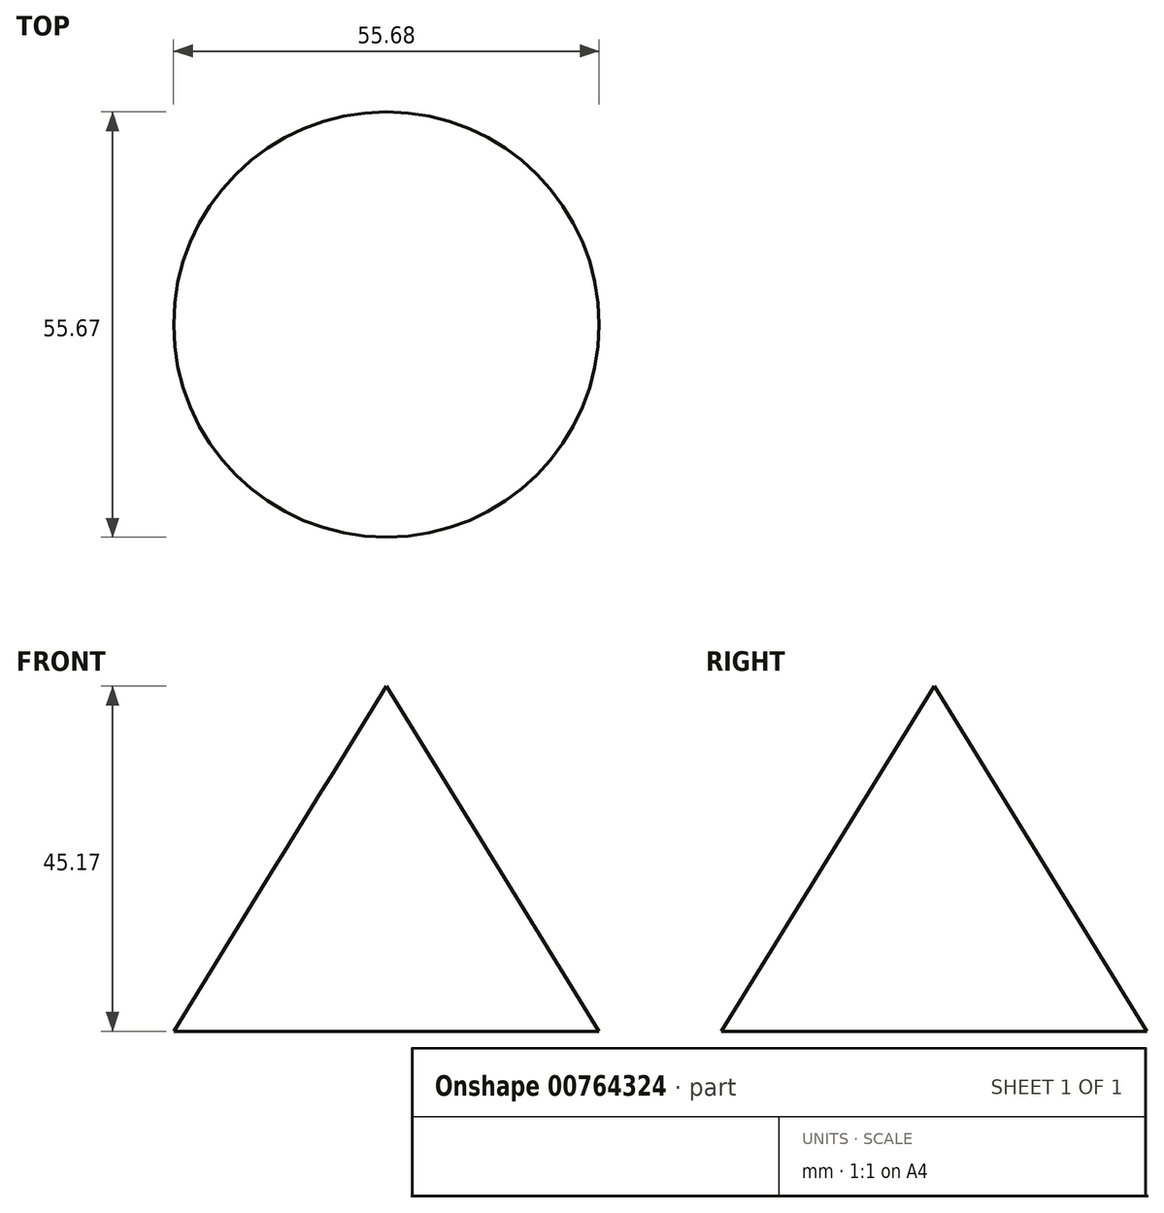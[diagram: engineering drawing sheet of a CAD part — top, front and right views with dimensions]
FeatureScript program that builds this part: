
annotation { "Feature Type Name" : "Feature", "Feature Type Description" : "" }
export const myFeature = defineFeature(function(context is Context, id is Id, definition is map)
    precondition{}
    {
        {
            var Q0;
            Q0=qCreatedBy(makeId("Right.planeOp"),FACE);
            var sketch = newSketch(context, id + "F0", { "sketchPlane" : qUnion([Q0])});
            skLineSegment(sketch, "E0", {"start": v(-38.25, 20.19) * mm, "end": v(-38.25, -24.98) * mm});
            skLineSegment(sketch, "E1", {"start": v(-10.42, -24.98) * mm, "end": v(-38.25, 20.19) * mm});
            skLineSegment(sketch, "E2", {"start": v(-10.42, -24.98) * mm, "end": v(-38.25, -24.98) * mm});
            skSolve(sketch);
        }
        {
            var Q0;
            Q0=makeQuery(id+"F0.imprint","IMPRINT",FACE,{"disambiguationData":[TD([[makeQuery(id+"F0.imprint","IMPRINT",EDGE,{"derivedFrom":sQuery(id+"F0.wireOp",EDGE,"E0")}),1.0]])]});
            var Q1;
            Q1=sQuery(id+"F0.wireOp",EDGE,"E0");
            revolve(context, id + "F1", {"surfaceOperationType" : NewSurfaceOperationType.NEW, "entities" : qUnion([Q0]), "axis" : qUnion([Q1]), "revolveType" : RevolveType.FULL});
        }
        {
            var Q0;
            Q0=qCreatedBy(makeId("Top.planeOp"),FACE);
            var sketch = newSketch(context, id + "F2", { "sketchPlane" : qUnion([Q0])});
            skLineSegment(sketch, "E3", {"start": v(-12.08, -8.02) * mm, "end": v(-12.08, -67.93) * mm});
            skSolve(sketch);
        }
        {
            var Q0;
            Q0=sQuery(id+"F2.wireOp",EDGE,"E3");
            extrude(context, id + "F3", {"bodyType" : ToolBodyType.SURFACE, "surfaceEntities" : qUnion([Q0]), "endBound" : BoundingType.SYMMETRIC, "depth" : 62.48 * mm, "offsetDistance" : 25.4 * mm});
        }
        {
            var Q0;
            Q0=qCreatedBy(makeId("Right.planeOp"),FACE);
            var sketch = newSketch(context, id + "F4", { "sketchPlane" : qUnion([Q0])});
            skLineSegment(sketch, "E4", {"start": v(-74.84, 3.68) * mm, "end": v(4.53, 3.68) * mm});
            skSolve(sketch);
        }
        {
            var Q0;
            Q0=sQuery(id+"F4.wireOp",EDGE,"E4");
            extrude(context, id + "F5", {"bodyType" : ToolBodyType.SURFACE, "surfaceEntities" : qUnion([Q0]), "endBound" : BoundingType.SYMMETRIC, "depth" : 142.24 * mm, "offsetDistance" : 25.4 * mm});
        }
    });
